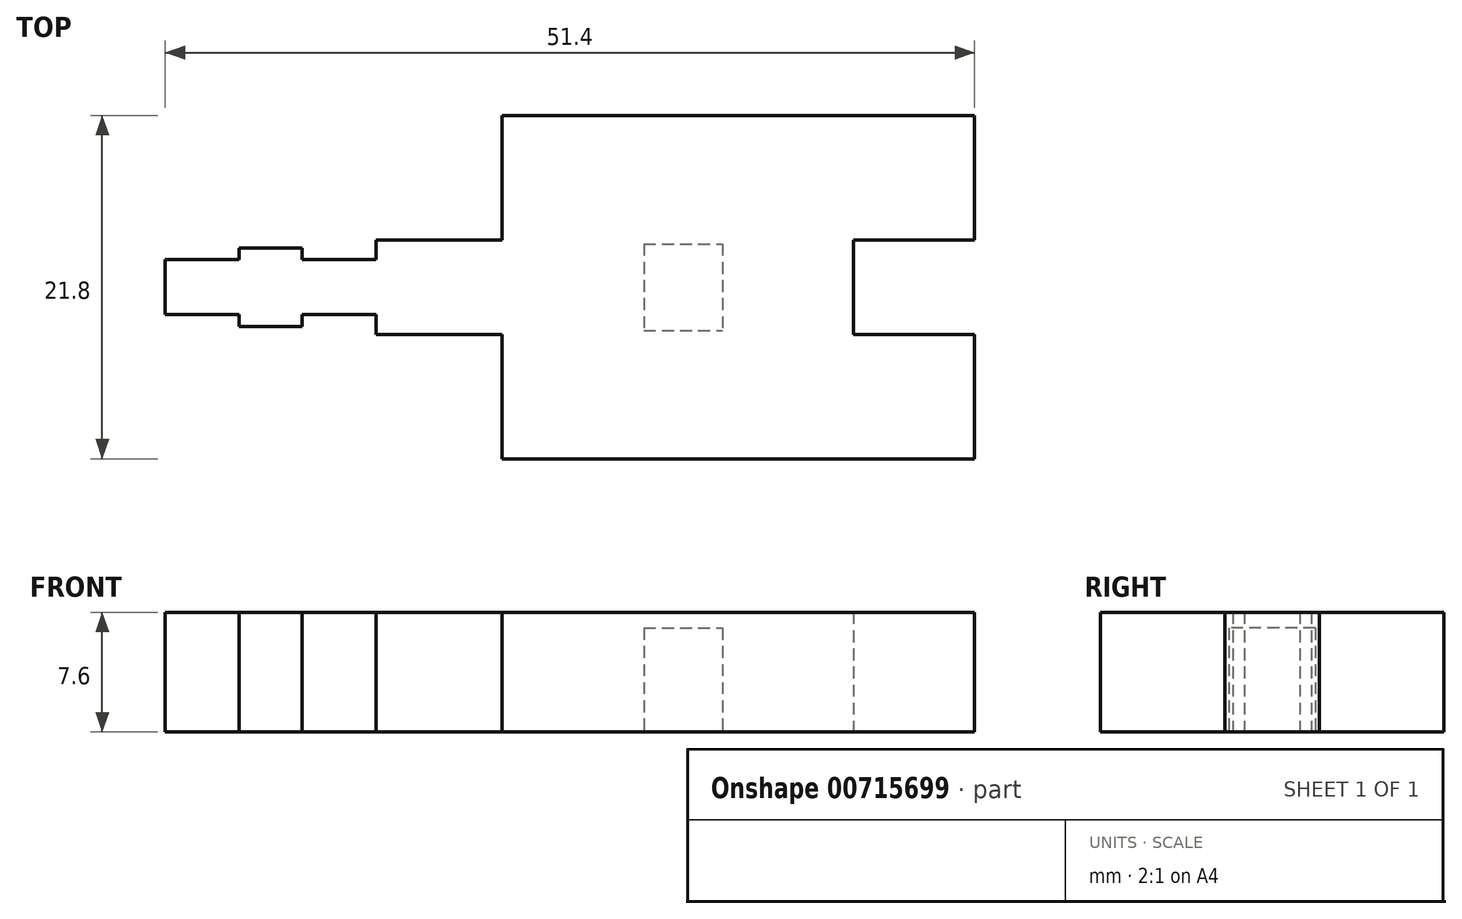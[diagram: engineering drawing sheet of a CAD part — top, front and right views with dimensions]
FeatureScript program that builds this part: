
annotation { "Feature Type Name" : "Feature", "Feature Type Description" : "" }
export const myFeature = defineFeature(function(context is Context, id is Id, definition is map)
    precondition{}
    {
        {
            var Q0;
            Q0=qCreatedBy(makeId("Top.planeOp"),FACE);
            var sketch = newSketch(context, id + "F0", { "sketchPlane" : qUnion([Q0])});
            skLineSegment(sketch, "E0.bottom", {"start": v(-15, -10.9) * mm, "end": v(15, -10.9) * mm});
            skLineSegment(sketch, "E0.top", {"start": v(-15, 10.9) * mm, "end": v(15, 10.9) * mm});
            skLineSegment(sketch, "E0.left", {"start": v(-15, -10.9) * mm, "end": v(-15, 10.9) * mm});
            skLineSegment(sketch, "E0.right", {"start": v(15, -10.9) * mm, "end": v(15, 10.9) * mm});
            skLineSegment(sketch, "E1", {"start": v(-15, 3) * mm, "end": v(-23, 3) * mm});
            skLineSegment(sketch, "E2", {"start": v(-23, 3) * mm, "end": v(-23, 1.75) * mm});
            skLineSegment(sketch, "E3", {"start": v(-23, 1.75) * mm, "end": v(-27.7, 1.75) * mm});
            skLineSegment(sketch, "E4", {"start": v(-27.7, 1.75) * mm, "end": v(-27.7, 2.5) * mm});
            skLineSegment(sketch, "E5", {"start": v(-27.7, 2.5) * mm, "end": v(-31.7, 2.5) * mm});
            skLineSegment(sketch, "E6", {"start": v(-31.7, 2.5) * mm, "end": v(-31.7, 1.75) * mm});
            skLineSegment(sketch, "E7", {"start": v(-31.7, 1.75) * mm, "end": v(-36.4, 1.75) * mm});
            skLineSegment(sketch, "E8", {"start": v(-36.4, 1.75) * mm, "end": v(-36.4, -1.75) * mm});
            skLineSegment(sketch, "E9", {"start": v(-36.4, -1.75) * mm, "end": v(-31.7, -1.75) * mm});
            skLineSegment(sketch, "E10", {"start": v(-31.7, -1.75) * mm, "end": v(-31.7, -2.5) * mm});
            skLineSegment(sketch, "E11", {"start": v(-31.7, -2.5) * mm, "end": v(-27.7, -2.5) * mm});
            skLineSegment(sketch, "E12", {"start": v(-27.7, -2.5) * mm, "end": v(-27.7, -1.75) * mm});
            skLineSegment(sketch, "E13", {"start": v(-27.7, -1.75) * mm, "end": v(-23, -1.75) * mm});
            skLineSegment(sketch, "E14", {"start": v(-23, -1.75) * mm, "end": v(-23, -3) * mm});
            skLineSegment(sketch, "E15", {"start": v(-23, -3) * mm, "end": v(-15, -3) * mm});
            skLineSegment(sketch, "E16.bottom", {"start": v(15, 3) * mm, "end": v(7.3, 3) * mm});
            skLineSegment(sketch, "E16.top", {"start": v(15, -3) * mm, "end": v(7.3, -3) * mm});
            skLineSegment(sketch, "E16.left", {"start": v(15, 3) * mm, "end": v(15, -3) * mm});
            skLineSegment(sketch, "E16.right", {"start": v(7.3, 3) * mm, "end": v(7.3, -3) * mm});
            skLineSegment(sketch, "E17.bottom", {"start": v(-6, 2.75) * mm, "end": v(-1, 2.75) * mm});
            skLineSegment(sketch, "E17.top", {"start": v(-6, -2.75) * mm, "end": v(-1, -2.75) * mm});
            skLineSegment(sketch, "E17.left", {"start": v(-6, 2.75) * mm, "end": v(-6, -2.75) * mm});
            skLineSegment(sketch, "E17.right", {"start": v(-1, 2.75) * mm, "end": v(-1, -2.75) * mm});
            skSolve(sketch);
        }
        {
            var Q0;
            {var subQ0=sQuery(id+"F0.wireOp",EDGE,"E1");Q0=makeQuery(id+"F0.imprint","IMPRINT",FACE,{"disambiguationData":[TD([[makeQuery(id+"F0.imprint","IMPRINT",EDGE,{"derivedFrom":subQ0}),1.0]])]});}
            var Q1;
            {var subQ4=sQuery(id+"F0.wireOp",EDGE,"E0.bottom");Q1=makeQuery(id+"F0.imprint","IMPRINT",FACE,{"disambiguationData":[TD([[makeQuery(id+"F0.imprint","IMPRINT",EDGE,{"derivedFrom":subQ4}),1.0]])]});}
            extrude(context, id + "F1", {"entities" : qUnion([Q0, Q1]), "depth" : 7.6 * mm, "offsetDistance" : 25 * mm});
        }
        {
            var Q0;
            Q0=makeQuery(id+"F1.opExtrude","CAP_FACE",FACE,{"disambiguationData":[OSD([sQuery(id+"F0.wireOp",EDGE,"E0.bottom"),sQuery(id+"F0.wireOp",EDGE,"E0.top"),sQuery(id+"F0.wireOp",EDGE,"E0.left"),sQuery(id+"F0.wireOp",EDGE,"E0.right"),sQuery(id+"F0.wireOp",EDGE,"E1"),sQuery(id+"F0.wireOp",EDGE,"E2"),sQuery(id+"F0.wireOp",EDGE,"E3"),sQuery(id+"F0.wireOp",EDGE,"E4"),sQuery(id+"F0.wireOp",EDGE,"E5"),sQuery(id+"F0.wireOp",EDGE,"E6"),sQuery(id+"F0.wireOp",EDGE,"E7"),sQuery(id+"F0.wireOp",EDGE,"E8"),sQuery(id+"F0.wireOp",EDGE,"E9"),sQuery(id+"F0.wireOp",EDGE,"E10"),sQuery(id+"F0.wireOp",EDGE,"E11"),sQuery(id+"F0.wireOp",EDGE,"E12"),sQuery(id+"F0.wireOp",EDGE,"E13"),sQuery(id+"F0.wireOp",EDGE,"E14"),sQuery(id+"F0.wireOp",EDGE,"E15"),sQuery(id+"F0.wireOp",EDGE,"E16.bottom"),sQuery(id+"F0.wireOp",EDGE,"E16.top"),sQuery(id+"F0.wireOp",EDGE,"E16.right"),sQuery(id+"F0.wireOp",EDGE,"E17.bottom"),sQuery(id+"F0.wireOp",EDGE,"E17.top"),sQuery(id+"F0.wireOp",EDGE,"E17.left"),sQuery(id+"F0.wireOp",EDGE,"E17.right")])],"isStart":false});
            var sketch = newSketch(context, id + "F2", { "sketchPlane" : qUnion([Q0])});
            skLineSegment(sketch, "E18.bottom", {"start": v(-8.4, -5.46) * mm, "end": v(2.13, -5.46) * mm});
            skLineSegment(sketch, "E18.top", {"start": v(-8.4, 5.08) * mm, "end": v(2.13, 5.08) * mm});
            skLineSegment(sketch, "E18.left", {"start": v(-8.4, -5.46) * mm, "end": v(-8.4, 5.08) * mm});
            skLineSegment(sketch, "E18.right", {"start": v(2.13, -5.46) * mm, "end": v(2.13, 5.08) * mm});
            skSolve(sketch);
        }
        {
            var Q0;
            Q0=makeQuery(id+"F2.imprint","IMPRINT",FACE,{"disambiguationData":[TD([[makeQuery(id+"F2.imprint","IMPRINT",EDGE,{"derivedFrom":makeQuery(id+"F1.opExtrude","CAP_EDGE",EDGE,{"disambiguationData":[OSD([sQuery(id+"F0.wireOp",EDGE,"E17.bottom")])],"isStart":false})}),-1.0]])]});
            extrude(context, id + "F3", {"entities" : qUnion([Q0]), "operationType" : NewBodyOperationType.ADD, "oppositeDirection" : true, "depth" : 1 * mm, "offsetDistance" : 25 * mm});
        }
    });
